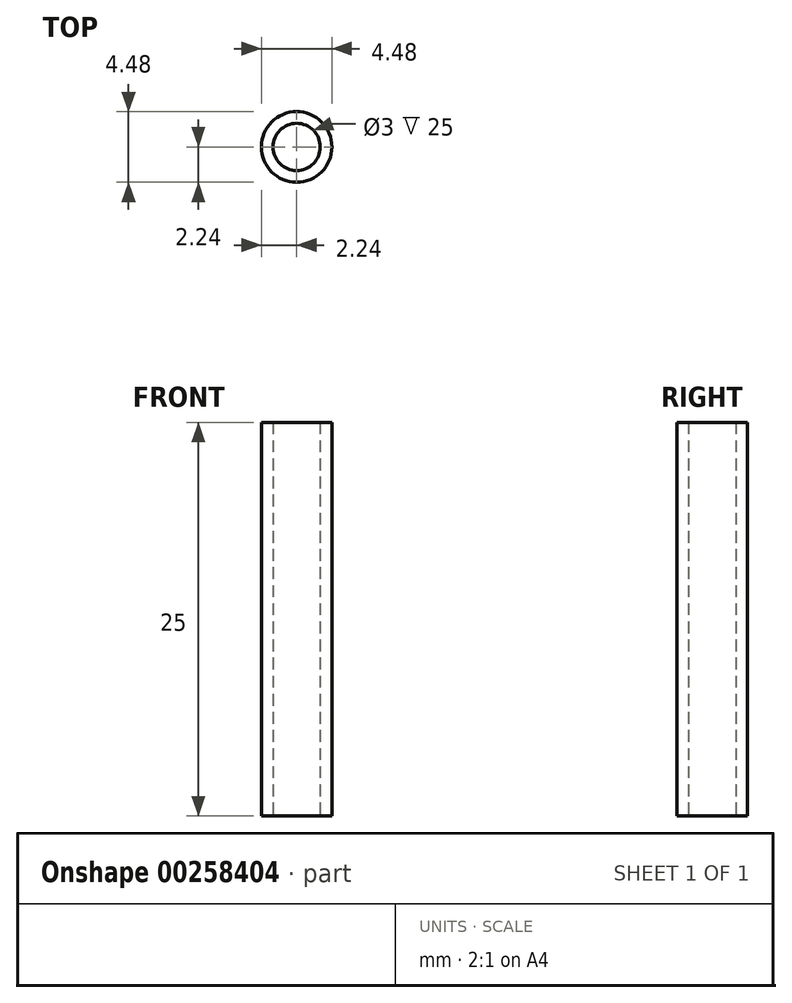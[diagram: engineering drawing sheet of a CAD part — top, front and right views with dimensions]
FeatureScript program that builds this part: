
annotation { "Feature Type Name" : "Feature", "Feature Type Description" : "" }
export const myFeature = defineFeature(function(context is Context, id is Id, definition is map)
    precondition{}
    {
        {
            var Q0;
            Q0=qCreatedBy(makeId("Top.planeOp"),FACE);
            var sketch = newSketch(context, id + "F0", { "sketchPlane" : qUnion([Q0])});
            skCircle(sketch, "E0", {"center": v(0, 0) * mm, "radius": 2.24 * mm});
            skCircle(sketch, "E1", {"center": v(0, 0) * mm, "radius": 1.5 * mm});
            skSolve(sketch);
        }
        {
            var Q0;
            Q0=makeQuery(id+"F0.imprint","IMPRINT",FACE,{"disambiguationData":[TD([[makeQuery(id+"F0.imprint","IMPRINT",EDGE,{"derivedFrom":sQuery(id+"F0.wireOp",EDGE,"E0")}),1.0]])]});
            extrude(context, id + "F1", {"entities" : qUnion([Q0]), "depth" : 25 * mm});
        }
    });
